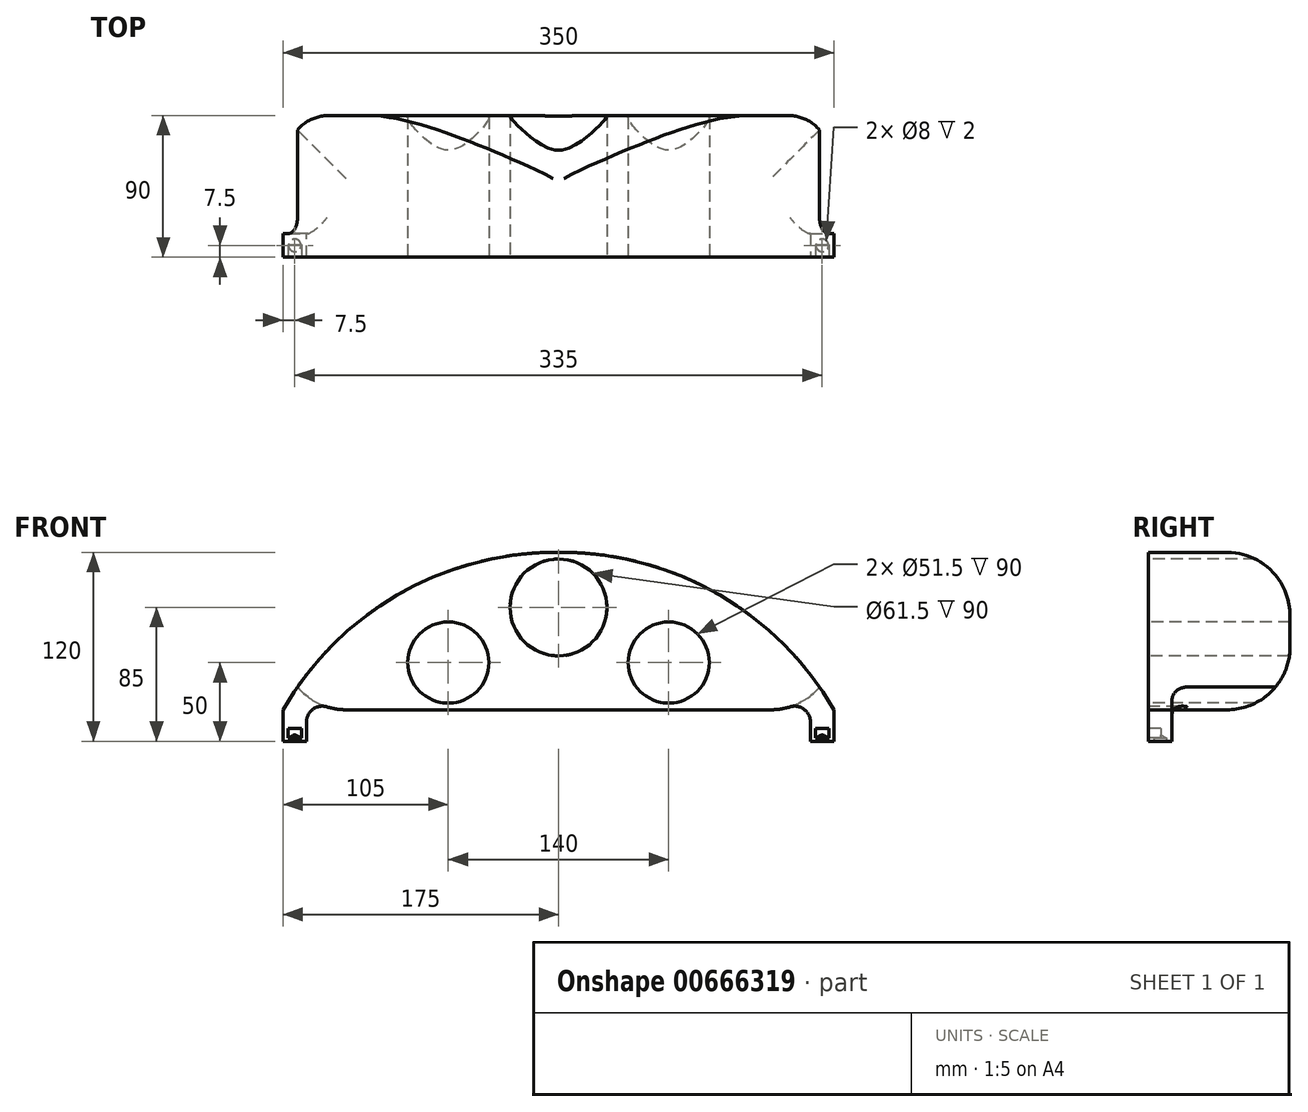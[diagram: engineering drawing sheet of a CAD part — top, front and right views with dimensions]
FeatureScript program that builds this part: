
annotation { "Feature Type Name" : "Feature", "Feature Type Description" : "" }
export const myFeature = defineFeature(function(context is Context, id is Id, definition is map)
    precondition{}
    {
        {
            var Q0;
            Q0=qCreatedBy(makeId("Top.planeOp"),FACE);
            var sketch = newSketch(context, id + "F0", { "sketchPlane" : qUnion([Q0])});
            skLineSegment(sketch, "E0.bottom", {"start": v(-175, 0) * mm, "end": v(-190, 0) * mm});
            skLineSegment(sketch, "E0.top", {"start": v(-175, 15) * mm, "end": v(-190, 15) * mm});
            skLineSegment(sketch, "E0.left", {"start": v(-175, 0) * mm, "end": v(-175, 15) * mm});
            skLineSegment(sketch, "E0.right", {"start": v(-190, 0) * mm, "end": v(-190, 15) * mm});
            skLineSegment(sketch, "E1.bottom", {"start": v(145, 0) * mm, "end": v(160, 0) * mm});
            skLineSegment(sketch, "E1.top", {"start": v(145, 15) * mm, "end": v(160, 15) * mm});
            skLineSegment(sketch, "E1.left", {"start": v(145, 0) * mm, "end": v(145, 15) * mm});
            skLineSegment(sketch, "E1.right", {"start": v(160, 0) * mm, "end": v(160, 15) * mm});
            skSolve(sketch);
        }
        {
            var Q0;
            Q0 = qSketchRegion(id + "F0", true);
            extrude(context, id + "F1", {"entities" : qUnion([Q0]), "depth" : 20 * mm, "offsetDistance" : 25 * mm});
        }
        {
            var Q0;
            Q0=makeQuery(id+"F1.opExtrude","CAP_FACE",FACE,{"disambiguationData":[OSD([sQuery(id+"F0.wireOp",EDGE,"E0.bottom"),sQuery(id+"F0.wireOp",EDGE,"E0.top"),sQuery(id+"F0.wireOp",EDGE,"E0.left"),sQuery(id+"F0.wireOp",EDGE,"E0.right")])],"isStart":false});
            var sketch = newSketch(context, id + "F2", { "sketchPlane" : qUnion([Q0])});
            skLineSegment(sketch, "E2.bottom", {"start": v(-190, 15) * mm, "end": v(160, 15) * mm});
            skLineSegment(sketch, "E2.top", {"start": v(-190, 0) * mm, "end": v(160, 0) * mm});
            skLineSegment(sketch, "E2.left", {"start": v(-190, 15) * mm, "end": v(-190, 0) * mm});
            skLineSegment(sketch, "E2.right", {"start": v(160, 15) * mm, "end": v(160, 0) * mm});
            skSolve(sketch);
        }
        {
            var Q0;
            Q0 = qSketchRegion(id + "F2", true);
            extrude(context, id + "F3", {"entities" : qUnion([Q0]), "depth" : 100 * mm, "offsetDistance" : 25 * mm});
        }
        {
            var Q0;
            Q0=makeQuery(id+"F1.opExtrude","SWEPT_BODY",BODY,{"disambiguationData":[OSD([sQuery(id+"F0.wireOp",EDGE,"E0.bottom"),sQuery(id+"F0.wireOp",EDGE,"E0.top"),sQuery(id+"F0.wireOp",EDGE,"E0.left"),sQuery(id+"F0.wireOp",EDGE,"E0.right")])]});
            var Q1;
            Q1=makeQuery(id+"F3.opExtrude","SWEPT_BODY",BODY,{"disambiguationData":[OSD([sQuery(id+"F2.wireOp",EDGE,"E2.bottom"),sQuery(id+"F2.wireOp",EDGE,"E2.top"),sQuery(id+"F2.wireOp",EDGE,"E2.left"),sQuery(id+"F2.wireOp",EDGE,"E2.right")])]});
            var Q2;
            Q2=makeQuery(id+"F1.opExtrude","SWEPT_BODY",BODY,{"disambiguationData":[OSD([sQuery(id+"F0.wireOp",EDGE,"E1.bottom"),sQuery(id+"F0.wireOp",EDGE,"E1.top"),sQuery(id+"F0.wireOp",EDGE,"E1.left"),sQuery(id+"F0.wireOp",EDGE,"E1.right")])]});
            booleanBodies(context, id + "F4", {"operationType" : BooleanOperationType.UNION, "tools" : qUnion([Q0, Q1, Q2])});
        }
        {
            var Q0;
            Q0=makeQuery(id+"F4.opBoolean","MERGE",FACE,{"derivedFrom":[makeQuery(id+"F1.opExtrude","SWEPT_FACE",FACE,{"disambiguationData":[OSD([sQuery(id+"F0.wireOp",EDGE,"E0.bottom")])]}),makeQuery(id+"F1.opExtrude","SWEPT_FACE",FACE,{"disambiguationData":[OSD([sQuery(id+"F0.wireOp",EDGE,"E1.bottom")])]}),makeQuery(id+"F3.opExtrude","SWEPT_FACE",FACE,{"disambiguationData":[OSD([sQuery(id+"F2.wireOp",EDGE,"E2.top")])]})]});
            var sketch = newSketch(context, id + "F5", { "sketchPlane" : qUnion([Q0])});
            skPoint(sketch, "E3", {"position": v(-15, 85) * mm});
            skPoint(sketch, "E3.positionSnap0", {"position": v(-15, 20) * mm});
            skPoint(sketch, "E4", {"position": v(-85, 50) * mm});
            skPoint(sketch, "E5", {"position": v(55, 50) * mm});
            skCircle(sketch, "E6", {"center": v(-15, 85) * mm, "radius": 30.75 * mm});
            skCircle(sketch, "E7", {"center": v(55, 50) * mm, "radius": 25.75 * mm});
            skCircle(sketch, "E8", {"center": v(-85, 50) * mm, "radius": 25.75 * mm});
            skArc(sketch, "E9", {"start": v(-15, 120) * mm, "mid": v(-116.02, 93.66) * mm, "end": v(-190, 20) * mm});
            skArc(sketch, "E10", {"start": v(160, 20) * mm, "mid": v(86.02, 93.66) * mm, "end": v(-15, 120) * mm});
            skSolve(sketch);
        }
        {
            var Q0;
            Q0 = qSketchRegion(id + "F5", true);
            extrude(context, id + "F6", {"entities" : qUnion([Q0]), "operationType" : NewBodyOperationType.REMOVE, "oppositeDirection" : true, "depth" : 25 * mm, "offsetDistance" : 25 * mm});
        }
        {
            var Q0;
            Q0 = qSketchRegion(id + "F5", true);
            extrude(context, id + "F7", {"entities" : qUnion([Q0]), "operationType" : NewBodyOperationType.REMOVE, "oppositeDirection" : true, "depth" : 25 * mm, "offsetDistance" : 25 * mm});
        }
        {
            var Q0;
            Q0=makeQuery(id+"F4.opBoolean","MERGE",FACE,{"derivedFrom":[makeQuery(id+"F1.opExtrude","SWEPT_FACE",FACE,{"disambiguationData":[OSD([sQuery(id+"F0.wireOp",EDGE,"E0.top")])]}),makeQuery(id+"F1.opExtrude","SWEPT_FACE",FACE,{"disambiguationData":[OSD([sQuery(id+"F0.wireOp",EDGE,"E1.top")])]}),makeQuery(id+"F3.opExtrude","SWEPT_FACE",FACE,{"disambiguationData":[OSD([sQuery(id+"F2.wireOp",EDGE,"E2.bottom")])]})]});
            var sketch = newSketch(context, id + "F8", { "sketchPlane" : qUnion([Q0])});
            skLineSegment(sketch, "E11", {"start": v(-145, 20) * mm, "end": v(-160, 20) * mm});
            skLineSegment(sketch, "E12", {"start": v(175, 20) * mm, "end": v(190, 20) * mm});
            skSolve(sketch);
        }
        {
            var Q0;
            {var subQ7=sQuery(id+"F8.wireOp",EDGE,"E11");Q0=makeQuery(id+"F8.imprint","IMPRINT",FACE,{"disambiguationData":[TD([[makeQuery(id+"F8.imprint","IMPRINT",EDGE,{"derivedFrom":subQ7}),-1.0]])]});}
            extrude(context, id + "F9", {"entities" : qUnion([Q0]), "operationType" : NewBodyOperationType.ADD, "depth" : 75 * mm, "offsetDistance" : 25 * mm});
        }
        {
            var Q0;
            {var subQ0=sQuery(id+"F2.wireOp",EDGE,"E2.right");Q0=makeQuery(id+"F9.boolean.opBoolean","MERGE",EDGE,{"derivedFrom":[makeQuery(id+"F3.opExtrude","CAP_EDGE",EDGE,{"disambiguationData":[OSD([subQ0])],"isStart":false}),makeQuery(id+"F9.opExtrude","SWEPT_EDGE",EDGE,{"disambiguationData":[OSD([sQuery(id+"F0.wireOp",EDGE,"E1.top"),sQuery(id+"F0.wireOp",EDGE,"E1.right"),sQuery(id+"F2.wireOp",EDGE,"E2.bottom"),subQ0])]})]});}
            var Q1;
            {var subQ0=sQuery(id+"F2.wireOp",EDGE,"E2.left");Q1=makeQuery(id+"F9.boolean.opBoolean","MERGE",EDGE,{"derivedFrom":[makeQuery(id+"F3.opExtrude","CAP_EDGE",EDGE,{"disambiguationData":[OSD([subQ0])],"isStart":false}),makeQuery(id+"F9.opExtrude","SWEPT_EDGE",EDGE,{"disambiguationData":[OSD([sQuery(id+"F0.wireOp",EDGE,"E0.top"),sQuery(id+"F0.wireOp",EDGE,"E0.right"),sQuery(id+"F2.wireOp",EDGE,"E2.bottom"),subQ0])]})]});}
            var Q2;
            Q2=makeQuery(id+"F9.opExtrude","SWEPT_EDGE",EDGE,{"disambiguationData":[OSD([sQuery(id+"F0.wireOp",EDGE,"E0.top"),sQuery(id+"F0.wireOp",EDGE,"E0.right"),sQuery(id+"F2.wireOp",EDGE,"E2.bottom"),sQuery(id+"F2.wireOp",EDGE,"E2.left"),sQuery(id+"F8.wireOp",EDGE,"E12")])]});
            var Q3;
            Q3=makeQuery(id+"F9.opExtrude","SWEPT_EDGE",EDGE,{"disambiguationData":[OSD([sQuery(id+"F0.wireOp",EDGE,"E1.top"),sQuery(id+"F0.wireOp",EDGE,"E1.right"),sQuery(id+"F2.wireOp",EDGE,"E2.bottom"),sQuery(id+"F2.wireOp",EDGE,"E2.right"),sQuery(id+"F8.wireOp",EDGE,"E11")])]});
            var Q4;
            Q4=makeQuery(id+"F9.opExtrude","CAP_EDGE",EDGE,{"disambiguationData":[OSD([sQuery(id+"F2.wireOp",EDGE,"E2.bottom")])],"isStart":false});
            var Q5;
            Q5=makeQuery(id+"F9.opExtrude","CAP_EDGE",EDGE,{"disambiguationData":[OSD([sQuery(id+"F2.wireOp",EDGE,"E2.bottom"),sQuery(id+"F8.wireOp",EDGE,"E11"),sQuery(id+"F8.wireOp",EDGE,"E12")])],"isStart":false});
            fillet(context, id + "F10", {"entities" : qUnion([Q0, Q1, Q2, Q3, Q4, Q5]), "radius" : 40 * mm, "tangentPropagation" : true, "allowEdgeOverflow" : false});
        }
        {
            var Q0;
            {var subQ0=sQuery(id+"F0.wireOp",EDGE,"E0.right");var subQ1=sQuery(id+"F2.wireOp",EDGE,"E2.left");var subQ2=sQuery(id+"F2.wireOp",EDGE,"E2.bottom");var subQ3=sQuery(id+"F0.wireOp",EDGE,"E0.left");var subQ4=sQuery(id+"F0.wireOp",EDGE,"E0.top");var subQ5=sQuery(id+"F8.wireOp",EDGE,"E12");Q0=makeQuery(id+"F10.opFillet","BLEND_EDGE",EDGE,{"blendedFrom":[makeQuery(id+"F9.opExtrude","SWEPT_EDGE",EDGE,{"disambiguationData":[OSD([subQ4,subQ0,subQ2,subQ1,subQ5])]}),makeQuery(id+"F9.boolean.opBoolean","SPLIT",FACE,{"disambiguationData":[TD([makeQuery(id+"F1.opExtrude","SWEPT_FACE",FACE,{"disambiguationData":[OSD([subQ3])]})])],"derivedFrom":makeQuery(id+"F4.opBoolean","MERGE",FACE,{"derivedFrom":[makeQuery(id+"F1.opExtrude","SWEPT_FACE",FACE,{"disambiguationData":[OSD([subQ4])]}),makeQuery(id+"F1.opExtrude","SWEPT_FACE",FACE,{"disambiguationData":[OSD([sQuery(id+"F0.wireOp",EDGE,"E1.top")])]}),makeQuery(id+"F3.opExtrude","SWEPT_FACE",FACE,{"disambiguationData":[OSD([subQ2])]})]})})],"blendedInto":[makeQuery(id+"F9.boolean.opBoolean","SPLIT",FACE,{"disambiguationData":[TD([makeQuery(id+"F1.opExtrude","SWEPT_FACE",FACE,{"disambiguationData":[OSD([subQ3])]})])],"derivedFrom":makeQuery(id+"F4.opBoolean","MERGE",FACE,{"derivedFrom":[makeQuery(id+"F1.opExtrude","SWEPT_FACE",FACE,{"disambiguationData":[OSD([subQ4])]}),makeQuery(id+"F1.opExtrude","SWEPT_FACE",FACE,{"disambiguationData":[OSD([sQuery(id+"F0.wireOp",EDGE,"E1.top")])]}),makeQuery(id+"F3.opExtrude","SWEPT_FACE",FACE,{"disambiguationData":[OSD([subQ2])]})]})})]});}
            var Q1;
            Q1=makeQuery(id+"F10.opFillet","BLEND_EDGE",EDGE,{"blendedFrom":[makeQuery(id+"F9.opExtrude","SWEPT_EDGE",EDGE,{"disambiguationData":[OSD([sQuery(id+"F0.wireOp",EDGE,"E0.top"),sQuery(id+"F0.wireOp",EDGE,"E0.right"),sQuery(id+"F2.wireOp",EDGE,"E2.bottom"),sQuery(id+"F2.wireOp",EDGE,"E2.left"),sQuery(id+"F8.wireOp",EDGE,"E12")])]}),makeQuery(id+"F1.opExtrude","SWEPT_FACE",FACE,{"disambiguationData":[OSD([sQuery(id+"F0.wireOp",EDGE,"E0.left")])]})],"blendedInto":[makeQuery(id+"F1.opExtrude","SWEPT_FACE",FACE,{"disambiguationData":[OSD([sQuery(id+"F0.wireOp",EDGE,"E0.left")])]})]});
            var Q2;
            Q2=makeQuery(id+"F10.opFillet","BLEND_EDGE",EDGE,{"blendedFrom":[makeQuery(id+"F9.opExtrude","SWEPT_EDGE",EDGE,{"disambiguationData":[OSD([sQuery(id+"F0.wireOp",EDGE,"E1.top"),sQuery(id+"F0.wireOp",EDGE,"E1.right"),sQuery(id+"F2.wireOp",EDGE,"E2.bottom"),sQuery(id+"F2.wireOp",EDGE,"E2.right"),sQuery(id+"F8.wireOp",EDGE,"E11")])]}),makeQuery(id+"F1.opExtrude","SWEPT_FACE",FACE,{"disambiguationData":[OSD([sQuery(id+"F0.wireOp",EDGE,"E1.left")])]})],"blendedInto":[makeQuery(id+"F1.opExtrude","SWEPT_FACE",FACE,{"disambiguationData":[OSD([sQuery(id+"F0.wireOp",EDGE,"E1.left")])]})]});
            var Q3;
            {var subQ0=sQuery(id+"F2.wireOp",EDGE,"E2.right");var subQ1=sQuery(id+"F2.wireOp",EDGE,"E2.bottom");var subQ2=sQuery(id+"F0.wireOp",EDGE,"E1.right");var subQ3=sQuery(id+"F0.wireOp",EDGE,"E1.left");var subQ4=sQuery(id+"F0.wireOp",EDGE,"E1.top");var subQ5=sQuery(id+"F8.wireOp",EDGE,"E11");Q3=makeQuery(id+"F10.opFillet","BLEND_EDGE",EDGE,{"blendedFrom":[makeQuery(id+"F9.opExtrude","SWEPT_EDGE",EDGE,{"disambiguationData":[OSD([subQ4,subQ2,subQ1,subQ0,subQ5])]}),makeQuery(id+"F9.boolean.opBoolean","SPLIT",FACE,{"disambiguationData":[TD([makeQuery(id+"F1.opExtrude","SWEPT_FACE",FACE,{"disambiguationData":[OSD([subQ3])]})])],"derivedFrom":makeQuery(id+"F4.opBoolean","MERGE",FACE,{"derivedFrom":[makeQuery(id+"F1.opExtrude","SWEPT_FACE",FACE,{"disambiguationData":[OSD([sQuery(id+"F0.wireOp",EDGE,"E0.top")])]}),makeQuery(id+"F1.opExtrude","SWEPT_FACE",FACE,{"disambiguationData":[OSD([subQ4])]}),makeQuery(id+"F3.opExtrude","SWEPT_FACE",FACE,{"disambiguationData":[OSD([subQ1])]})]})})],"blendedInto":[makeQuery(id+"F9.boolean.opBoolean","SPLIT",FACE,{"disambiguationData":[TD([makeQuery(id+"F1.opExtrude","SWEPT_FACE",FACE,{"disambiguationData":[OSD([subQ3])]})])],"derivedFrom":makeQuery(id+"F4.opBoolean","MERGE",FACE,{"derivedFrom":[makeQuery(id+"F1.opExtrude","SWEPT_FACE",FACE,{"disambiguationData":[OSD([sQuery(id+"F0.wireOp",EDGE,"E0.top")])]}),makeQuery(id+"F1.opExtrude","SWEPT_FACE",FACE,{"disambiguationData":[OSD([subQ4])]}),makeQuery(id+"F3.opExtrude","SWEPT_FACE",FACE,{"disambiguationData":[OSD([subQ1])]})]})})]});}
            fillet(context, id + "F11", {"entities" : qUnion([Q0, Q1, Q2, Q3]), "radius" : 10 * mm, "tangentPropagation" : true, "allowEdgeOverflow" : false});
        }
        {
            var Q0;
            Q0=makeQuery(id+"F4.opBoolean","MERGE",FACE,{"derivedFrom":[makeQuery(id+"F1.opExtrude","SWEPT_FACE",FACE,{"disambiguationData":[OSD([sQuery(id+"F0.wireOp",EDGE,"E0.bottom")])]}),makeQuery(id+"F1.opExtrude","SWEPT_FACE",FACE,{"disambiguationData":[OSD([sQuery(id+"F0.wireOp",EDGE,"E1.bottom")])]}),makeQuery(id+"F3.opExtrude","SWEPT_FACE",FACE,{"disambiguationData":[OSD([sQuery(id+"F2.wireOp",EDGE,"E2.top")])]})]});
            var sketch = newSketch(context, id + "F12", { "sketchPlane" : qUnion([Q0])});
            skLineSegment(sketch, "E13.bottom", {"start": v(-186.75, 8) * mm, "end": v(-178.25, 8) * mm});
            skLineSegment(sketch, "E13.top", {"start": v(-186.75, 2) * mm, "end": v(-178.25, 2) * mm});
            skLineSegment(sketch, "E13.left", {"start": v(-186.75, 8) * mm, "end": v(-186.75, 2) * mm});
            skLineSegment(sketch, "E13.right", {"start": v(-178.25, 8) * mm, "end": v(-178.25, 2) * mm});
            skLineSegment(sketch, "E14.bottom", {"start": v(148.25, 8) * mm, "end": v(156.75, 8) * mm});
            skLineSegment(sketch, "E14.top", {"start": v(148.25, 2) * mm, "end": v(156.75, 2) * mm});
            skLineSegment(sketch, "E14.left", {"start": v(148.25, 8) * mm, "end": v(148.25, 2) * mm});
            skLineSegment(sketch, "E14.right", {"start": v(156.75, 8) * mm, "end": v(156.75, 2) * mm});
            skSolve(sketch);
        }
        {
            var Q0;
            Q0 = qSketchRegion(id + "F12", true);
            extrude(context, id + "F13", {"entities" : qUnion([Q0]), "operationType" : NewBodyOperationType.REMOVE, "oppositeDirection" : true, "depth" : 8 * mm, "offsetDistance" : 25 * mm});
        }
        {
            var Q0;
            Q0=makeQuery(id+"F1.opExtrude","CAP_FACE",FACE,{"disambiguationData":[OSD([sQuery(id+"F0.wireOp",EDGE,"E0.bottom"),sQuery(id+"F0.wireOp",EDGE,"E0.top"),sQuery(id+"F0.wireOp",EDGE,"E0.left"),sQuery(id+"F0.wireOp",EDGE,"E0.right")])],"isStart":true});
            var sketch = newSketch(context, id + "F14", { "sketchPlane" : qUnion([Q0])});
            skPoint(sketch, "E15", {"position": v(-182.5, -7.5) * mm});
            skPoint(sketch, "E15.positionSnap0", {"position": v(-175, -7.5) * mm});
            skPoint(sketch, "E15.positionSnap1", {"position": v(-182.5, 0) * mm});
            skSolve(sketch);
        }
        {
            var Q0;
            Q0=makeQuery(id+"F1.opExtrude","CAP_FACE",FACE,{"disambiguationData":[OSD([sQuery(id+"F0.wireOp",EDGE,"E1.bottom"),sQuery(id+"F0.wireOp",EDGE,"E1.top"),sQuery(id+"F0.wireOp",EDGE,"E1.left"),sQuery(id+"F0.wireOp",EDGE,"E1.right")])],"isStart":true});
            var sketch = newSketch(context, id + "F15", { "sketchPlane" : qUnion([Q0])});
            skPoint(sketch, "E16", {"position": v(152.5, -7.5) * mm});
            skPoint(sketch, "E16.positionSnap0", {"position": v(160, -7.5) * mm});
            skPoint(sketch, "E16.positionSnap1", {"position": v(152.5, 0) * mm});
            skSolve(sketch);
        }
        {
            var Q0;
            Q0=sQuery(id+"F15.wireOp",VERTEX,"E16");
            var Q1;
            Q1=sQuery(id+"F14.wireOp",VERTEX,"E15");
            var Q2;
            Q2=makeQuery(id+"F1.opExtrude","SWEPT_BODY",BODY,{"disambiguationData":[OSD([sQuery(id+"F0.wireOp",EDGE,"E0.bottom"),sQuery(id+"F0.wireOp",EDGE,"E0.top"),sQuery(id+"F0.wireOp",EDGE,"E0.left"),sQuery(id+"F0.wireOp",EDGE,"E0.right")])]});
            hole(context, id + "F16", {"style" : HoleStyle.SIMPLE, "endStyle" : HoleEndStyle.BLIND, "holeDiameter" : 8 * mm, "majorDiameter" : 5 * mm, "holeDepth" : 2 * mm, "isTappedThrough" : true, "tappedDepth" : 12 * mm, "tapClearance" : 3, "startFromSketch" : true, "locations" : qUnion([Q0, Q1]), "scope" : qUnion([Q2])});
        }
        {
            var Q0;
            {var subQ0=sQuery(id+"F5.wireOp",EDGE,"E9");Q0=makeQuery(id+"F5.imprint","IMPRINT",FACE,{"disambiguationData":[TD([[makeQuery(id+"F5.imprint","IMPRINT",EDGE,{"derivedFrom":subQ0}),-1.0]])]});}
            var Q1;
            {var subQ0=sQuery(id+"F5.wireOp",EDGE,"E10");Q1=makeQuery(id+"F5.imprint","IMPRINT",FACE,{"disambiguationData":[TD([[makeQuery(id+"F5.imprint","IMPRINT",EDGE,{"derivedFrom":subQ0}),-1.0]])]});}
            extrude(context, id + "F17", {"entities" : qUnion([Q0, Q1]), "operationType" : NewBodyOperationType.REMOVE, "oppositeDirection" : true, "depth" : 200 * mm, "offsetDistance" : 25 * mm});
        }
    });
